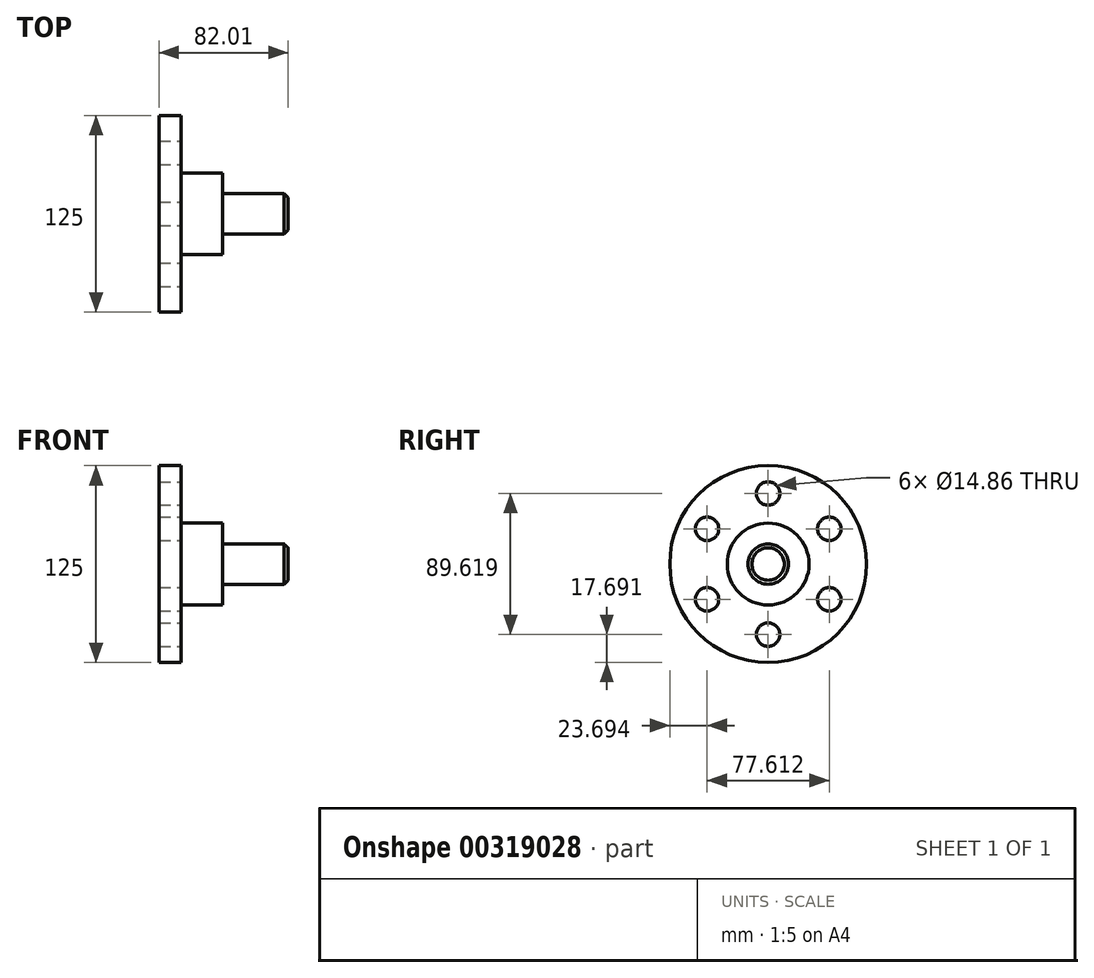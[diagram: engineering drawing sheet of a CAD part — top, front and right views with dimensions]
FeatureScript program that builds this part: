
annotation { "Feature Type Name" : "Feature", "Feature Type Description" : "" }
export const myFeature = defineFeature(function(context is Context, id is Id, definition is map)
    precondition{}
    {
        {
            var Q0;
            Q0=qCreatedBy(makeId("Front.planeOp"),FACE);
            var sketch = newSketch(context, id + "F0", { "sketchPlane" : qUnion([Q0])});
            skLineSegment(sketch, "E0", {"start": v(0, 0) * mm, "end": v(82, 0) * mm});
            skLineSegment(sketch, "E1", {"start": v(82, 0) * mm, "end": v(82, 12.84) * mm});
            skLineSegment(sketch, "E2", {"start": v(82, 12.84) * mm, "end": v(40.34, 12.84) * mm});
            skLineSegment(sketch, "E3", {"start": v(40.34, 12.84) * mm, "end": v(40.34, 25.97) * mm});
            skLineSegment(sketch, "E4", {"start": v(40.34, 25.97) * mm, "end": v(14.08, 25.97) * mm});
            skLineSegment(sketch, "E5", {"start": v(14.08, 25.97) * mm, "end": v(14.08, 62.5) * mm});
            skLineSegment(sketch, "E6", {"start": v(14.08, 62.5) * mm, "end": v(0, 62.5) * mm});
            skLineSegment(sketch, "E7", {"start": v(0, 62.5) * mm, "end": v(0, 0) * mm});
            skSolve(sketch);
        }
        {
            var Q0;
            Q0=makeQuery(id+"F0.imprint","IMPRINT",FACE,{"disambiguationData":[TD([[makeQuery(id+"F0.imprint","IMPRINT",EDGE,{"derivedFrom":sQuery(id+"F0.wireOp",EDGE,"E0")}),1.0]])]});
            var Q1;
            Q1=sQuery(id+"F0.wireOp",EDGE,"E0");
            revolve(context, id + "F1", {"entities" : qUnion([Q0]), "axis" : qUnion([Q1]), "revolveType" : RevolveType.FULL});
        }
        {
            var Q0;
            Q0=makeQuery(id+"F1.opRevolve","SWEPT_EDGE",EDGE,{"disambiguationData":[OSD([sQuery(id+"F0.wireOp",EDGE,"E1"),sQuery(id+"F0.wireOp",EDGE,"E2")])]});
            chamfer(context, id + "F2", {"entities" : qUnion([Q0]), "width" : 2.54 * mm, "tangentPropagation" : true});
        }
        {
            var Q0;
            Q0=makeQuery(id+"F1.opRevolve","SWEPT_FACE",FACE,{"disambiguationData":[OSD([sQuery(id+"F0.wireOp",EDGE,"E5")])]});
            var sketch = newSketch(context, id + "F3", { "sketchPlane" : qUnion([Q0])});
            skCircle(sketch, "E8", {"center": v(0, 44.8) * mm, "radius": 7.43 * mm});
            skPoint(sketch, "E9.center", {"position": v(0, 0) * mm});
            skCircle(sketch, "E10.1.0", {"center": v(-38.8, 22.4) * mm, "radius": 7.43 * mm});
            skCircle(sketch, "E10.2.0", {"center": v(-38.8, -22.4) * mm, "radius": 7.43 * mm});
            skCircle(sketch, "E10.3.0", {"center": v(0, -44.8) * mm, "radius": 7.43 * mm});
            skCircle(sketch, "E10.4.0", {"center": v(38.8, -22.4) * mm, "radius": 7.43 * mm});
            skCircle(sketch, "E10.5.0", {"center": v(38.8, 22.4) * mm, "radius": 7.43 * mm});
            skSolve(sketch);
        }
        {
            var Q0;
            Q0 = qSketchRegion(id + "F3", true);
            extrude(context, id + "F4", {"entities" : qUnion([Q0]), "operationType" : NewBodyOperationType.REMOVE, "oppositeDirection" : true, "depth" : 25.4 * mm});
        }
    });
